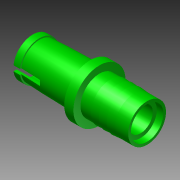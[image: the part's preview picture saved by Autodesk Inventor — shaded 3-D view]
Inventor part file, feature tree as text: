
AUTODESK INVENTOR PART (.ipt)
format: ipt  version: 2015 (Build 190159000, 159)  size: 166,400 bytes
history: native  units: in
note: dims shown in document units (in); Inventor stores cm internally (conversion verified against a paired STEP export)
features: hole x2, sketch x2, revolve x1, extrude x1
ambient origin geometry x8: Origin, YZ Plane, XZ Plane, XY Plane, X Axis, Y Axis, Z Axis, Center Point
bodies: Solid1 (feature_tree)
feature tree (6):
  revolve  "Revolution1"  [1 undecoded]
  extrude  "Extrusion1"  Depth=0.375in
  hole  "Hole1"  [1 undecoded]
  hole  "Hole2"  [1 undecoded]
  sketch  "Sketch1"  dims[d0=0.07in d1=0.4in]
  sketch  "Sketch2"  dims[d2=0.365in d3=0.29in d4=0.3in d5=0.1in d6=0.06in d7=0.3in d8=0.3in d9=0.44in d10=0.28in d11=0.05in d12=90.0deg d13=0.04in d14=0.2in d15=1.0in d16=0.0in d17=1.0in d18=1.0in d19=0.1875in d20=0.75in d21=0.25in d22=0.25in d23=0.5635in d24=0.4375in d25=0.0in d26=1.0in d27=1.0in d28=0.1875in d29=0.75in d30=0.25in d31=0.05in d32=0.5635in d33=0.375in d34=0.0in]
note: 3 required parameter values undecoded (feature->parameter linkage not recoverable at this tier; creation-order binding heuristic only, values carry confidence <= 0.55)